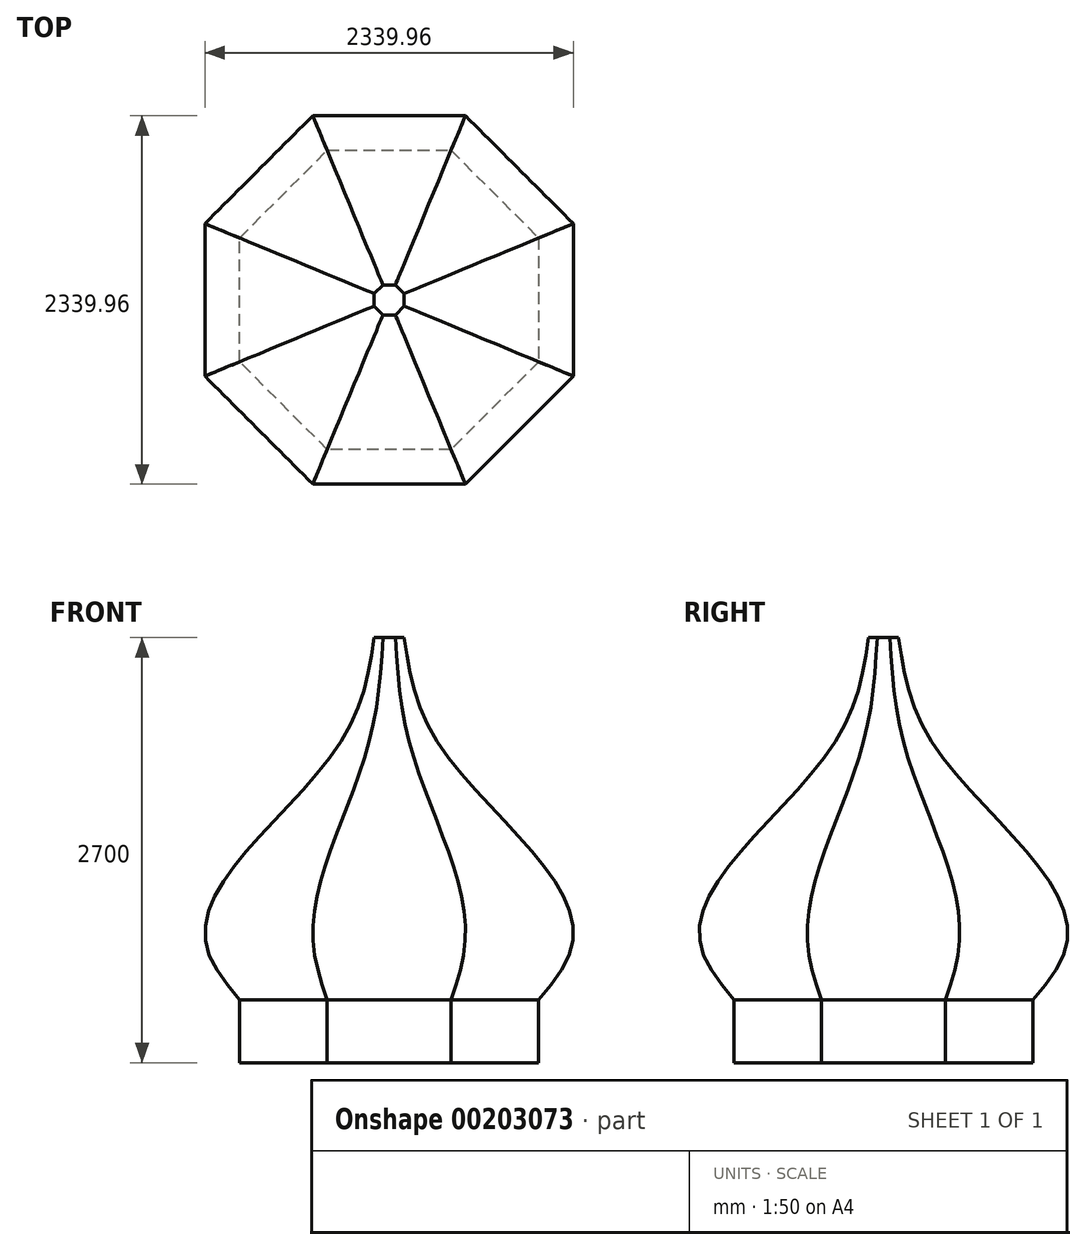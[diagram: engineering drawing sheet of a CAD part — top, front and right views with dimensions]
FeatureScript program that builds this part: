
annotation { "Feature Type Name" : "Feature", "Feature Type Description" : "" }
export const myFeature = defineFeature(function(context is Context, id is Id, definition is map)
    precondition{}
    {
        {
            assignVariable(context, id + "F0", {"name" : "height", "anyValue" : 2700});
        }
        {
            assignVariable(context, id + "F1", {"name" : "small", "anyValue" : getVariable(context, 'height') * 0.8});
        }
        {
            assignVariable(context, id + "F2", {"name" : "large", "anyValue" : getVariable(context, 'height') * 0.25});
        }
        {
            var Q0;
            Q0=qCreatedBy(makeId("Top.planeOp"),FACE);
            cPlane(context, id + "F3", {"entities" : qUnion([Q0]), "cplaneType" : CPlaneType.OFFSET, "offset" : 400 * mm, "width" : 150 * mm, "height" : 150 * mm});
        }
        {
            var Q0;
            Q0=qCreatedBy(makeId("Top.planeOp"),FACE);
            cPlane(context, id + "F4", {"entities" : qUnion([Q0]), "cplaneType" : CPlaneType.OFFSET, "offset" : (getVariable(context, 'large')) * mm, "width" : 150 * mm, "height" : 150 * mm});
        }
        {
            var Q0;
            Q0=qCreatedBy(makeId("Top.planeOp"),FACE);
            cPlane(context, id + "F5", {"entities" : qUnion([Q0]), "cplaneType" : CPlaneType.OFFSET, "offset" : (getVariable(context, 'small')) * mm, "width" : 150 * mm, "height" : 150 * mm});
        }
        {
            var Q0;
            Q0=qCreatedBy(makeId("Top.planeOp"),FACE);
            cPlane(context, id + "F6", {"entities" : qUnion([Q0]), "cplaneType" : CPlaneType.OFFSET, "offset" : (getVariable(context, 'height')) * mm, "width" : 150 * mm, "height" : 150 * mm});
        }
        {
            var Q0;
            Q0=qCreatedBy(makeId("Top.planeOp"),FACE);
            var sketch = newSketch(context, id + "F7", { "sketchPlane" : qUnion([Q0])});
            skCircle(sketch, "E0.cCircle", {"center": v(0, 0) * mm, "radius": 950 * mm, "construction": true});
            skLineSegment(sketch, "E0.0", {"start": v(950, -393.5) * mm, "end": v(393.5, -950) * mm});
            skLineSegment(sketch, "E0.1", {"start": v(393.5, -950) * mm, "end": v(-393.5, -950) * mm});
            skLineSegment(sketch, "E0.2", {"start": v(-393.5, -950) * mm, "end": v(-950, -393.5) * mm});
            skLineSegment(sketch, "E0.3", {"start": v(-950, -393.5) * mm, "end": v(-950, 393.5) * mm});
            skLineSegment(sketch, "E0.4", {"start": v(-950, 393.5) * mm, "end": v(-393.5, 950) * mm});
            skLineSegment(sketch, "E0.5", {"start": v(-393.5, 950) * mm, "end": v(393.5, 950) * mm});
            skLineSegment(sketch, "E0.6", {"start": v(393.5, 950) * mm, "end": v(950, 393.5) * mm});
            skLineSegment(sketch, "E0.7", {"start": v(950, 393.5) * mm, "end": v(950, -393.5) * mm});
            skPoint(sketch, "E0.0.midPoint", {"position": v(671.75, -671.75) * mm});
            skLineSegment(sketch, "E1", {"start": v(0, 0) * mm, "end": v(0, 1334.8) * mm, "construction": true});
            skSolve(sketch);
        }
        {
            var Q0;
            Q0=qCreatedBy(id+"F3.planeOp",FACE);
            var sketch = newSketch(context, id + "F8", { "sketchPlane" : qUnion([Q0])});
            skCircle(sketch, "E2.cCircle", {"center": v(0, 0) * mm, "radius": 950 * mm, "construction": true});
            skLineSegment(sketch, "E2.0", {"start": v(950, -393.5) * mm, "end": v(393.5, -950) * mm});
            skLineSegment(sketch, "E2.1", {"start": v(393.5, -950) * mm, "end": v(-393.5, -950) * mm});
            skLineSegment(sketch, "E2.2", {"start": v(-393.5, -950) * mm, "end": v(-950, -393.5) * mm});
            skLineSegment(sketch, "E2.3", {"start": v(-950, -393.5) * mm, "end": v(-950, 393.5) * mm});
            skLineSegment(sketch, "E2.4", {"start": v(-950, 393.5) * mm, "end": v(-393.5, 950) * mm});
            skLineSegment(sketch, "E2.5", {"start": v(-393.5, 950) * mm, "end": v(393.5, 950) * mm});
            skLineSegment(sketch, "E2.6", {"start": v(393.5, 950) * mm, "end": v(950, 393.5) * mm});
            skLineSegment(sketch, "E2.7", {"start": v(950, 393.5) * mm, "end": v(950, -393.5) * mm});
            skPoint(sketch, "E2.0.midPoint", {"position": v(671.75, -671.75) * mm});
            skLineSegment(sketch, "E3", {"start": v(0, 0) * mm, "end": v(0, 1338.4) * mm, "construction": true});
            skSolve(sketch);
        }
        {
            var Q0;
            Q0=qCreatedBy(id+"F4.planeOp",FACE);
            var sketch = newSketch(context, id + "F9", { "sketchPlane" : qUnion([Q0])});
            skCircle(sketch, "E4.cCircle", {"center": v(0, 0) * mm, "radius": 1140 * mm, "construction": true});
            skLineSegment(sketch, "E4.0", {"start": v(1140, -472.2) * mm, "end": v(472.2, -1140) * mm});
            skLineSegment(sketch, "E4.1", {"start": v(472.2, -1140) * mm, "end": v(-472.2, -1140) * mm});
            skLineSegment(sketch, "E4.2", {"start": v(-472.2, -1140) * mm, "end": v(-1140, -472.2) * mm});
            skLineSegment(sketch, "E4.3", {"start": v(-1140, -472.2) * mm, "end": v(-1140, 472.2) * mm});
            skLineSegment(sketch, "E4.4", {"start": v(-1140, 472.2) * mm, "end": v(-472.2, 1140) * mm});
            skLineSegment(sketch, "E4.5", {"start": v(-472.2, 1140) * mm, "end": v(472.2, 1140) * mm});
            skLineSegment(sketch, "E4.6", {"start": v(472.2, 1140) * mm, "end": v(1140, 472.2) * mm});
            skLineSegment(sketch, "E4.7", {"start": v(1140, 472.2) * mm, "end": v(1140, -472.2) * mm});
            skPoint(sketch, "E4.0.midPoint", {"position": v(806.1, -806.1) * mm});
            skLineSegment(sketch, "E5", {"start": v(0, 0) * mm, "end": v(0, 758.1) * mm, "construction": true});
            skSolve(sketch);
        }
        {
            var Q0;
            Q0=qCreatedBy(id+"F5.planeOp",FACE);
            var sketch = newSketch(context, id + "F10", { "sketchPlane" : qUnion([Q0])});
            skCircle(sketch, "E6.cCircle", {"center": v(0, 0) * mm, "radius": 237.5 * mm, "construction": true});
            skLineSegment(sketch, "E6.0", {"start": v(237.5, -98.38) * mm, "end": v(98.38, -237.5) * mm});
            skLineSegment(sketch, "E6.1", {"start": v(98.38, -237.5) * mm, "end": v(-98.38, -237.5) * mm});
            skLineSegment(sketch, "E6.2", {"start": v(-98.38, -237.5) * mm, "end": v(-237.5, -98.38) * mm});
            skLineSegment(sketch, "E6.3", {"start": v(-237.5, -98.38) * mm, "end": v(-237.5, 98.38) * mm});
            skLineSegment(sketch, "E6.4", {"start": v(-237.5, 98.38) * mm, "end": v(-98.38, 237.5) * mm});
            skLineSegment(sketch, "E6.5", {"start": v(-98.38, 237.5) * mm, "end": v(98.38, 237.5) * mm});
            skLineSegment(sketch, "E6.6", {"start": v(98.38, 237.5) * mm, "end": v(237.5, 98.38) * mm});
            skLineSegment(sketch, "E6.7", {"start": v(237.5, 98.38) * mm, "end": v(237.5, -98.38) * mm});
            skPoint(sketch, "E6.0.midPoint", {"position": v(167.94, -167.94) * mm});
            skLineSegment(sketch, "E7", {"start": v(0, 0) * mm, "end": v(0, 894.79) * mm, "construction": true});
            skSolve(sketch);
        }
        {
            var Q0;
            Q0=qCreatedBy(id+"F6.planeOp",FACE);
            var sketch = newSketch(context, id + "F11", { "sketchPlane" : qUnion([Q0])});
            skCircle(sketch, "E8.cCircle", {"center": v(0, 0) * mm, "radius": 95 * mm, "construction": true});
            skLineSegment(sketch, "E8.0", {"start": v(95, -39.35) * mm, "end": v(39.35, -95) * mm});
            skLineSegment(sketch, "E8.1", {"start": v(39.35, -95) * mm, "end": v(-39.35, -95) * mm});
            skLineSegment(sketch, "E8.2", {"start": v(-39.35, -95) * mm, "end": v(-95, -39.35) * mm});
            skLineSegment(sketch, "E8.3", {"start": v(-95, -39.35) * mm, "end": v(-95, 39.35) * mm});
            skLineSegment(sketch, "E8.4", {"start": v(-95, 39.35) * mm, "end": v(-39.35, 95) * mm});
            skLineSegment(sketch, "E8.5", {"start": v(-39.35, 95) * mm, "end": v(39.35, 95) * mm});
            skLineSegment(sketch, "E8.6", {"start": v(39.35, 95) * mm, "end": v(95, 39.35) * mm});
            skLineSegment(sketch, "E8.7", {"start": v(95, 39.35) * mm, "end": v(95, -39.35) * mm});
            skPoint(sketch, "E8.0.midPoint", {"position": v(67.18, -67.18) * mm});
            skLineSegment(sketch, "E9", {"start": v(0, 0) * mm, "end": v(0, 749.04) * mm, "construction": true});
            skSolve(sketch);
        }
        {
            var Q0;
            Q0=makeQuery(id+"F8.imprint","IMPRINT",FACE,{"disambiguationData":[TD([[makeQuery(id+"F8.imprint","IMPRINT",EDGE,{"derivedFrom":sQuery(id+"F8.wireOp",EDGE,"E2.0")}),-1.0]])]});
            var Q1;
            Q1=makeQuery(id+"F9.imprint","IMPRINT",FACE,{"disambiguationData":[TD([[makeQuery(id+"F9.imprint","IMPRINT",EDGE,{"derivedFrom":sQuery(id+"F9.wireOp",EDGE,"E4.0")}),-1.0]])]});
            var Q2;
            Q2=makeQuery(id+"F10.imprint","IMPRINT",FACE,{"disambiguationData":[TD([[makeQuery(id+"F10.imprint","IMPRINT",EDGE,{"derivedFrom":sQuery(id+"F10.wireOp",EDGE,"E6.0")}),-1.0]])]});
            var Q3;
            Q3=makeQuery(id+"F11.imprint","IMPRINT",FACE,{"disambiguationData":[TD([[makeQuery(id+"F11.imprint","IMPRINT",EDGE,{"derivedFrom":sQuery(id+"F11.wireOp",EDGE,"E8.0")}),-1.0]])]});
            loft(context, id + "F12", {"sheetProfilesArray" : [{ "sheetProfileEntities" : qUnion([Q0]) }, { "sheetProfileEntities" : qUnion([Q1]) }, { "sheetProfileEntities" : qUnion([Q2]) }, { "sheetProfileEntities" : qUnion([Q3]) }]});
        }
        {
            var Q1;
            Q1=makeQuery(id+"F8.imprint","IMPRINT",FACE,{"disambiguationData":[TD([[makeQuery(id+"F8.imprint","IMPRINT",EDGE,{"derivedFrom":sQuery(id+"F8.wireOp",EDGE,"E2.0")}),-1.0]])]});
            var Q2;
            Q2=makeQuery(id+"F7.imprint","IMPRINT",FACE,{"disambiguationData":[TD([[makeQuery(id+"F7.imprint","IMPRINT",EDGE,{"derivedFrom":sQuery(id+"F7.wireOp",EDGE,"E0.0")}),-1.0]])]});
            loft(context, id + "F13", {"operationType" : NewBodyOperationType.ADD, "sheetProfilesArray" : [{ "sheetProfileEntities" : qUnion([Q1]) }, { "sheetProfileEntities" : qUnion([Q2]) }]});
        }
    });
